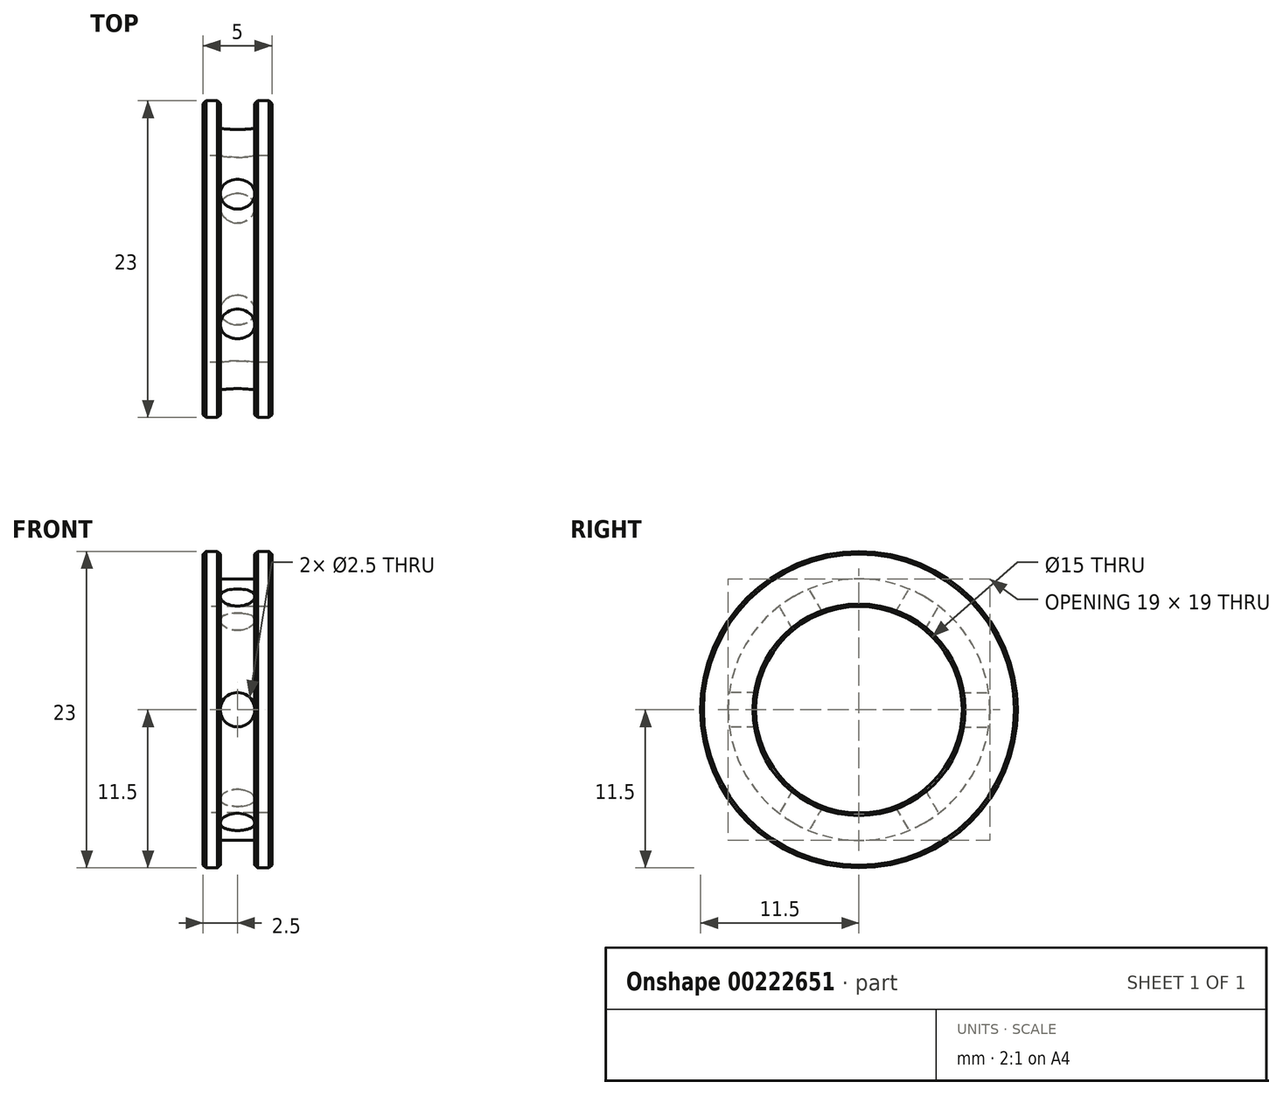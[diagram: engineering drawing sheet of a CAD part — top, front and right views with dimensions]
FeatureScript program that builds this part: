
annotation { "Feature Type Name" : "Feature", "Feature Type Description" : "" }
export const myFeature = defineFeature(function(context is Context, id is Id, definition is map)
    precondition{}
    {
        {
            var Q0;
            Q0=qCreatedBy(makeId("Top.planeOp"),FACE);
            var sketch = newSketch(context, id + "F0", { "sketchPlane" : qUnion([Q0])});
            skLineSegment(sketch, "E0", {"start": v(0, -7.5) * mm, "end": v(2.5, -7.5) * mm});
            skLineSegment(sketch, "E1", {"start": v(2.5, -7.5) * mm, "end": v(2.5, -11.5) * mm});
            skLineSegment(sketch, "E2", {"start": v(2.5, -11.5) * mm, "end": v(1.25, -11.5) * mm});
            skLineSegment(sketch, "E3", {"start": v(1.25, -11.5) * mm, "end": v(1.25, -9.5) * mm});
            skLineSegment(sketch, "E4", {"start": v(1.25, -9.5) * mm, "end": v(0, -9.5) * mm});
            skLineSegment(sketch, "E5", {"start": v(1.25, 13) * mm, "end": v(1.25, 4) * mm});
            skLineSegment(sketch, "E6", {"start": v(1.25, 4) * mm, "end": v(0, 4) * mm});
            skLineSegment(sketch, "E7", {"start": v(1.25, 13) * mm, "end": v(0, 13) * mm});
            skLineSegment(sketch, "E8.MirrorCS", {"start": v(-1.25, -11.5) * mm, "end": v(-1.25, -9.5) * mm});
            skLineSegment(sketch, "E9.MirrorCS", {"start": v(-2.5, -11.5) * mm, "end": v(-1.25, -11.5) * mm});
            skLineSegment(sketch, "E10.MirrorCS", {"start": v(-2.5, -7.5) * mm, "end": v(-2.5, -11.5) * mm});
            skLineSegment(sketch, "E11.MirrorCS", {"start": v(0, -7.5) * mm, "end": v(-2.5, -7.5) * mm});
            skLineSegment(sketch, "E12.MirrorCS", {"start": v(-1.25, -9.5) * mm, "end": v(0, -9.5) * mm});
            skLineSegment(sketch, "E13", {"start": v(-38.92, 0) * mm, "end": v(51.03, 0) * mm});
            skLineSegment(sketch, "E14", {"start": v(0, 13) * mm, "end": v(0, 4) * mm});
            skSolve(sketch);
        }
        {
            var Q0;
            Q0=makeQuery(id+"F0.imprint","IMPRINT",FACE,{"disambiguationData":[TD([[makeQuery(id+"F0.imprint","IMPRINT",EDGE,{"derivedFrom":sQuery(id+"F0.wireOp",EDGE,"E0")}),-1.0]])]});
            var Q1;
            Q1=sQuery(id+"F0.wireOp",EDGE,"E13");
            revolve(context, id + "F1", {"entities" : qUnion([Q0]), "axis" : qUnion([Q1]), "revolveType" : RevolveType.FULL});
        }
        {
            var Q0;
            Q0=makeQuery(id+"F0.imprint","IMPRINT",FACE,{"disambiguationData":[TD([[makeQuery(id+"F0.imprint","IMPRINT",EDGE,{"derivedFrom":sQuery(id+"F0.wireOp",EDGE,"E5")}),-1.0]])]});
            var Q1;
            Q1=sQuery(id+"F0.wireOp",EDGE,"E14");
            revolve(context, id + "F2", {"entities" : qUnion([Q0]), "axis" : qUnion([Q1]), "revolveType" : RevolveType.FULL});
        }
        {
            var Q0;
            Q0=makeQuery(id+"F2.opRevolve","SWEPT_BODY",BODY,{"disambiguationData":[OSD([sQuery(id+"F0.wireOp",EDGE,"E5"),sQuery(id+"F0.wireOp",EDGE,"E6"),sQuery(id+"F0.wireOp",EDGE,"E7"),sQuery(id+"F0.wireOp",EDGE,"E14")])]});
            var Q1;
            Q1=sQuery(id+"F0.wireOp",EDGE,"E13");
            circularPattern(context, id + "F3", {"entities" : qUnion([Q0]), "axis" : qUnion([Q1]), "angle" : 360 * degree, "instanceCount" : 6, "equalSpace" : true});
        }
        {
            var Q0;
            Q0=makeQuery(id+"F2.opRevolve","SWEPT_BODY",BODY,{"disambiguationData":[OSD([sQuery(id+"F0.wireOp",EDGE,"E5"),sQuery(id+"F0.wireOp",EDGE,"E6"),sQuery(id+"F0.wireOp",EDGE,"E7"),sQuery(id+"F0.wireOp",EDGE,"E14")])]});
            var Q1;
            Q1=makeQuery(id+"F3.opPattern","COPY",BODY,{"derivedFrom":makeQuery(id+"F2.opRevolve","SWEPT_BODY",BODY,{"disambiguationData":[OSD([sQuery(id+"F0.wireOp",EDGE,"E5"),sQuery(id+"F0.wireOp",EDGE,"E6"),sQuery(id+"F0.wireOp",EDGE,"E7"),sQuery(id+"F0.wireOp",EDGE,"E14")])]}),"instanceName":"2"});
            var Q2;
            Q2=makeQuery(id+"F3.opPattern","COPY",BODY,{"derivedFrom":makeQuery(id+"F2.opRevolve","SWEPT_BODY",BODY,{"disambiguationData":[OSD([sQuery(id+"F0.wireOp",EDGE,"E5"),sQuery(id+"F0.wireOp",EDGE,"E6"),sQuery(id+"F0.wireOp",EDGE,"E7"),sQuery(id+"F0.wireOp",EDGE,"E14")])]}),"instanceName":"1"});
            var Q3;
            Q3=makeQuery(id+"F3.opPattern","COPY",BODY,{"derivedFrom":makeQuery(id+"F2.opRevolve","SWEPT_BODY",BODY,{"disambiguationData":[OSD([sQuery(id+"F0.wireOp",EDGE,"E5"),sQuery(id+"F0.wireOp",EDGE,"E6"),sQuery(id+"F0.wireOp",EDGE,"E7"),sQuery(id+"F0.wireOp",EDGE,"E14")])]}),"instanceName":"3"});
            var Q4;
            Q4=makeQuery(id+"F3.opPattern","COPY",BODY,{"derivedFrom":makeQuery(id+"F2.opRevolve","SWEPT_BODY",BODY,{"disambiguationData":[OSD([sQuery(id+"F0.wireOp",EDGE,"E5"),sQuery(id+"F0.wireOp",EDGE,"E6"),sQuery(id+"F0.wireOp",EDGE,"E7"),sQuery(id+"F0.wireOp",EDGE,"E14")])]}),"instanceName":"4"});
            var Q5;
            Q5=makeQuery(id+"F3.opPattern","COPY",BODY,{"derivedFrom":makeQuery(id+"F2.opRevolve","SWEPT_BODY",BODY,{"disambiguationData":[OSD([sQuery(id+"F0.wireOp",EDGE,"E5"),sQuery(id+"F0.wireOp",EDGE,"E6"),sQuery(id+"F0.wireOp",EDGE,"E7"),sQuery(id+"F0.wireOp",EDGE,"E14")])]}),"instanceName":"5"});
            var Q6;
            Q6=makeQuery(id+"F1.opRevolve","SWEPT_BODY",BODY,{"disambiguationData":[OSD([sQuery(id+"F0.wireOp",EDGE,"E0"),sQuery(id+"F0.wireOp",EDGE,"E1"),sQuery(id+"F0.wireOp",EDGE,"E2"),sQuery(id+"F0.wireOp",EDGE,"E3"),sQuery(id+"F0.wireOp",EDGE,"E4"),sQuery(id+"F0.wireOp",EDGE,"E8.MirrorCS"),sQuery(id+"F0.wireOp",EDGE,"E9.MirrorCS"),sQuery(id+"F0.wireOp",EDGE,"E10.MirrorCS"),sQuery(id+"F0.wireOp",EDGE,"E11.MirrorCS"),sQuery(id+"F0.wireOp",EDGE,"E12.MirrorCS")])]});
            booleanBodies(context, id + "F4", {"operationType" : BooleanOperationType.SUBTRACTION, "tools" : qUnion([Q0, Q1, Q2, Q3, Q4, Q5]), "targets" : qUnion([Q6])});
        }
        {
            var Q0;
            Q0=makeQuery(id+"F1.opRevolve","SWEPT_EDGE",EDGE,{"disambiguationData":[OSD([sQuery(id+"F0.wireOp",EDGE,"E1"),sQuery(id+"F0.wireOp",EDGE,"E2")])]});
            var Q1;
            Q1=makeQuery(id+"F1.opRevolve","SWEPT_EDGE",EDGE,{"disambiguationData":[OSD([sQuery(id+"F0.wireOp",EDGE,"E9.MirrorCS"),sQuery(id+"F0.wireOp",EDGE,"E10.MirrorCS")])]});
            chamfer(context, id + "F5", {"entities" : qUnion([Q0, Q1]), "width" : 0.2 * mm, "tangentPropagation" : true});
        }
        {
            var Q0;
            Q0=makeQuery(id+"F1.opRevolve","SWEPT_EDGE",EDGE,{"disambiguationData":[OSD([sQuery(id+"F0.wireOp",EDGE,"E8.MirrorCS"),sQuery(id+"F0.wireOp",EDGE,"E9.MirrorCS")])]});
            var Q1;
            Q1=makeQuery(id+"F1.opRevolve","SWEPT_EDGE",EDGE,{"disambiguationData":[OSD([sQuery(id+"F0.wireOp",EDGE,"E2"),sQuery(id+"F0.wireOp",EDGE,"E3")])]});
            var Q2;
            Q2=makeQuery(id+"F1.opRevolve","SWEPT_EDGE",EDGE,{"disambiguationData":[OSD([sQuery(id+"F0.wireOp",EDGE,"E0"),sQuery(id+"F0.wireOp",EDGE,"E1")])]});
            var Q3;
            Q3=makeQuery(id+"F1.opRevolve","SWEPT_EDGE",EDGE,{"disambiguationData":[OSD([sQuery(id+"F0.wireOp",EDGE,"E10.MirrorCS"),sQuery(id+"F0.wireOp",EDGE,"E11.MirrorCS")])]});
            chamfer(context, id + "F6", {"entities" : qUnion([Q0, Q1, Q2, Q3]), "width" : 0.2 * mm, "tangentPropagation" : true});
        }
    });
